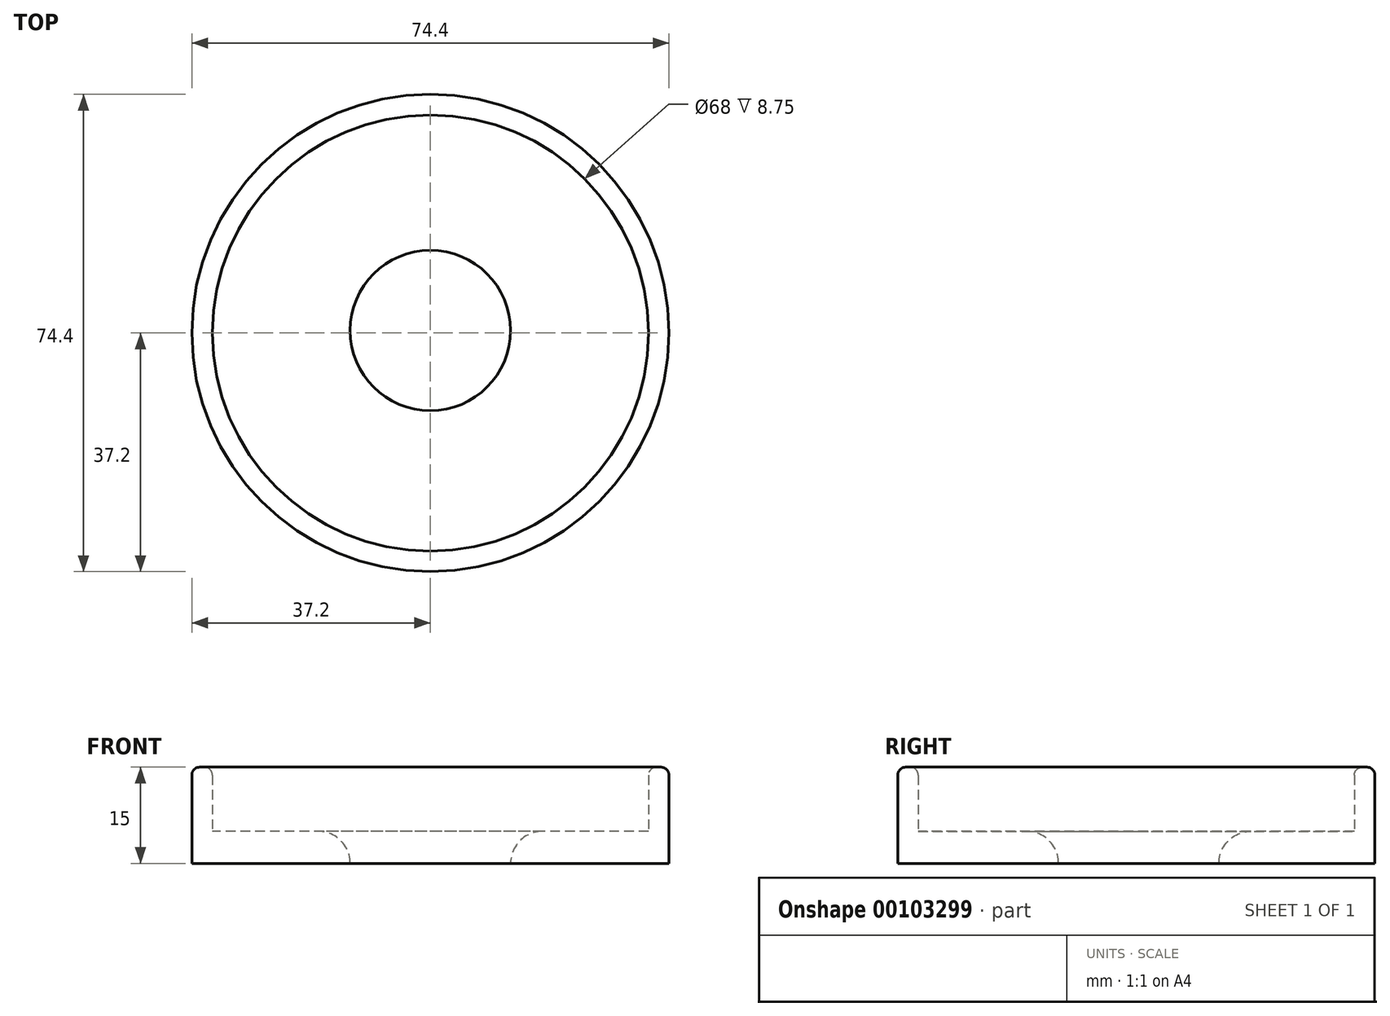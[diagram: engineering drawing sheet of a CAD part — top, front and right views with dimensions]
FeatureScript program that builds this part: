
annotation { "Feature Type Name" : "Feature", "Feature Type Description" : "" }
export const myFeature = defineFeature(function(context is Context, id is Id, definition is map)
    precondition{}
    {
        {
            var Q0;
            Q0=qCreatedBy(makeId("Top.planeOp"),FACE);
            var sketch = newSketch(context, id + "F0", { "sketchPlane" : qUnion([Q0])});
            skCircle(sketch, "E0", {"center": v(0, 0) * mm, "radius": 37.2 * mm});
            skCircle(sketch, "E1", {"center": v(0, 0) * mm, "radius": 34 * mm});
            skCircle(sketch, "E2", {"center": v(0, 0.38) * mm, "radius": 12.5 * mm});
            skSolve(sketch);
        }
        {
            var Q0;
            Q0=makeQuery(id+"F0.imprint","IMPRINT",FACE,{"disambiguationData":[TD([[makeQuery(id+"F0.imprint","IMPRINT",EDGE,{"derivedFrom":sQuery(id+"F0.wireOp",EDGE,"E1")}),1.0]])]});
            extrude(context, id + "F1", {"entities" : qUnion([Q0]), "depth" : 5 * mm});
        }
        {
            var Q0;
            Q0=makeQuery(id+"F0.imprint","IMPRINT",FACE,{"disambiguationData":[TD([[makeQuery(id+"F0.imprint","IMPRINT",EDGE,{"derivedFrom":sQuery(id+"F0.wireOp",EDGE,"E0")}),1.0]])]});
            extrude(context, id + "F2", {"entities" : qUnion([Q0]), "operationType" : NewBodyOperationType.ADD, "depth" : 15 * mm});
        }
        {
            var Q0;
            Q0=makeQuery(id+"F2.opExtrude","CAP_EDGE",EDGE,{"disambiguationData":[OSD([sQuery(id+"F0.wireOp",EDGE,"E1")])],"isStart":false});
            var Q1;
            Q1=makeQuery(id+"F2.opExtrude","CAP_EDGE",EDGE,{"disambiguationData":[OSD([sQuery(id+"F0.wireOp",EDGE,"E0")])],"isStart":false});
            fillet(context, id + "F3", {"entities" : qUnion([Q0, Q1]), "radius" : 1.25 * mm, "tangentPropagation" : true, "allowEdgeOverflow" : false});
        }
        {
            var Q0;
            Q0=makeQuery(id+"F1.opExtrude","CAP_EDGE",EDGE,{"disambiguationData":[OSD([sQuery(id+"F0.wireOp",EDGE,"E2")])],"isStart":false});
            fillet(context, id + "F4", {"entities" : qUnion([Q0]), "radius" : 5 * mm, "tangentPropagation" : true, "allowEdgeOverflow" : false});
        }
    });
